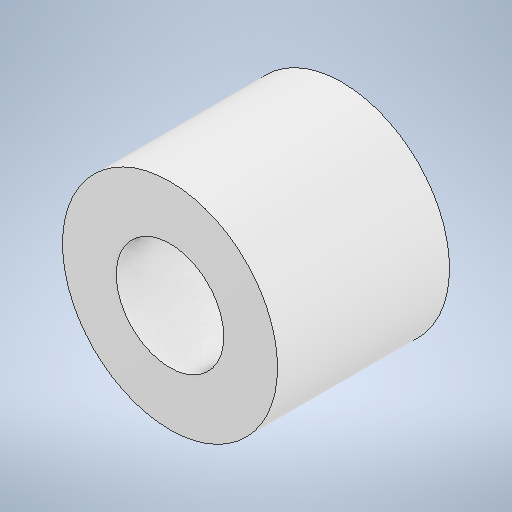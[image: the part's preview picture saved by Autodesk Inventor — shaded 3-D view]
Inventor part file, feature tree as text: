
AUTODESK INVENTOR PART (.ipt)
format: ipt  version: 2025.1 (Build 291241020, 241B)  size: 353,280 bytes
history: native  units: mm
features: extrude x1, sketch x1
ambient origin geometry x8: Origin, YZ Plane, XZ Plane, XY Plane, X Axis, Y Axis, Z Axis, Center Point
bodies: Solid1 (feature_tree)
feature tree (2):
  extrude  "Extrusion1"  Depth=4.0mm
  sketch  "Sketch1"  dims[d0=2.5mm d1=5.0mm d2=4.0mm d3=0.0mm]
